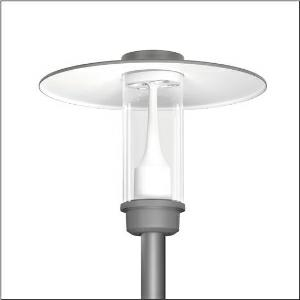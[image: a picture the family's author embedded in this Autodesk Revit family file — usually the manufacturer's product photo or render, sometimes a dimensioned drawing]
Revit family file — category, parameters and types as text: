
# Revit family: litepole_2_iq___pl1_2s_5xa5425cf14h_8640
name_source: partatom
category: Lighting Fixtures
units: mm (PartAtom-declared; Revit-internal decimal feet)

## family parameters
Cut with Voids When Loaded = No
Host = Face
Light Source = No
Part Type = Normal
Room Calculation Point = No
Round Connector Dimension = Use Diameter
Shared = No

## types (1)
- --- (1 x LED, 2990 lm, 23.9 W, 2200K)
    Apparent Load = 24 VA
    CIE Flux Codes = 22 60 92 98 100
    Color Rendering = 70
    Color Temperature = 2200K
    Default Elevation = 1800 mm
    Description = Litepole 2 iQ, mast luminaire, Module 540 iQ-SR, primary light control with 3 zone facetted reflector, of plastic, silver coated, highly specular, structured, primary optical cover: cover, of PMMA, transparent, light distribution: PL1.2s, light emission: direct distribution, primary light characteristic: symmetric, installation type: post-top, LED, High Power LED, rated luminous flux: 2.990lm, luminous efficacy: 125lm/W, light colour: 722, colour temperature: 2200K, control gear: iQ Street-Remote, control: pre-setting: logarithmic dimming characteristic, Street-Remote, Auto-Match, Temp-Guard, Lumen-Switch, Night-Set, Smart-Wire, Light-Fading, Desk-Remote (wireless, voltage-free reading and setting of iQ features in the workshop via application-optimized NFC function/RFID function), optimised constant luminous flux control (CLO 2.0), with terminal, 6-pole, max. 2.5mm², mains connection: 230..240V, AC, 50/60Hz, start of lifetime: 24W, end of service life: 26W, reduction: 12W, luminaire housing, upper part, of aluminium, coated, Siteco® metallic grey (DB 702S), diameter: 750mm, height: 590mm, spigot size: d x l = 76 x 70mm (post-top) | with reducer (optional accessory) 60 x 70mm, mounting height: 3..5m, post-top mast mounting element, of diecast aluminium, coated, Siteco® metallic grey (DB 702S), Module 540 iQ-SR, traffic white (RAL 9016), equipment: standard, protection rating (complete): IP65, insulation class (complete): insulation class II (safety insulation), certification: CE, ENEC, VDE, packaging unit: 1 piece

Light Distribution: PL1.2s
    Height = 590 mm
    Lamp = 1 x LED
    Lamp Light Flux = 2990 lm
    Lamp Power = 23.9 W
    Lamp count = 1
    Length = 750 mm
    Luminous efficacy = 125 lm/W
    Manufacturer = Siteco
    ModVariant = No
    Model = 5XA5425CF14H
    Number of Poles = 1
    OnlyDefault = Yes
    Power Factor = 1
    Product Name = Litepole 2 iQ | PL1.2s
    Product group = mast luminaire | pylon top
    ProductGroupID = 6100
    Protection Class = Protection class II
    Protection Degree = IP 65
    RLX_Detail_Level = 1
    RLX_Emergency_Light_Flux = 0 lm
    RLX_Emergency_Type = 0
    RLX_Emergency_Type_DB = No
    RlxData = <blob elided: 29509 chars, md5=a2734679>
    Socket = socket
    Standby Power = 0 W
    System Light Flux = 2990 lm
    System Power = 24 W
    Type Comments = factory setting: luminous flux: 100 % | dim-lin: 254 | 499 mA
    Type Image = l_1006518.jpg
    URL = http://relux.com
    VarID = @adj_144177
    Voltage = 0 V
    Weight = 0.00 kg
    Width = 0 mm  [stored 0 ft]

note: [stored X ft] marks values corroborated as IEEE doubles in the binary element streams (Revit-internal decimal feet)

## geometry (parser evidence)
native form markers: Blend x4, Sweep x8
no freeform markers — native parametric forms only
